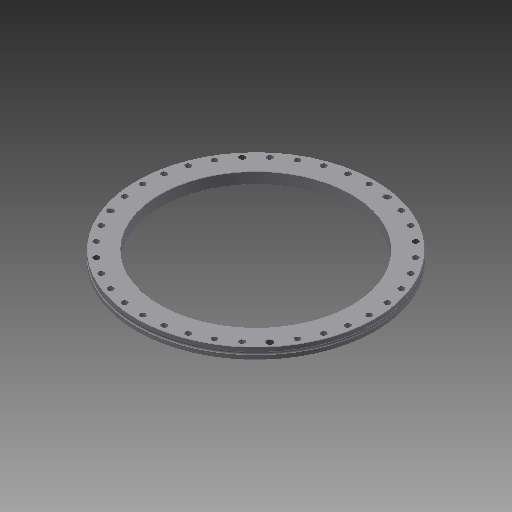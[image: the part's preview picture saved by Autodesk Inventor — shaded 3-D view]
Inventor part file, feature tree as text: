
AUTODESK INVENTOR PART (.ipt)
format: ipt  version: 2019 (Build 230136000, 136)  size: 184,832 bytes
history: native  units: in
note: dims shown in document units (in); Inventor stores cm internally (conversion verified against a paired STEP export)
features: thread x4, other x1
ambient origin geometry x8: Origin, YZ Plane, XZ Plane, XY Plane, X Axis, Y Axis, Z Axis, Center Point
bodies: Solid1 (feature_tree)
feature tree (5):
  thread  "Thread1"  [1 undecoded]
  thread  "Thread4"  [1 undecoded]
  thread  "Thread5"  [1 undecoded]
  thread  "Thread6"  [1 undecoded]
  other  "bearing_nrt_260_b_0_02.ipt"
note: 4 required parameter values undecoded (feature->parameter linkage not recoverable at this tier; creation-order binding heuristic only, values carry confidence <= 0.55)
